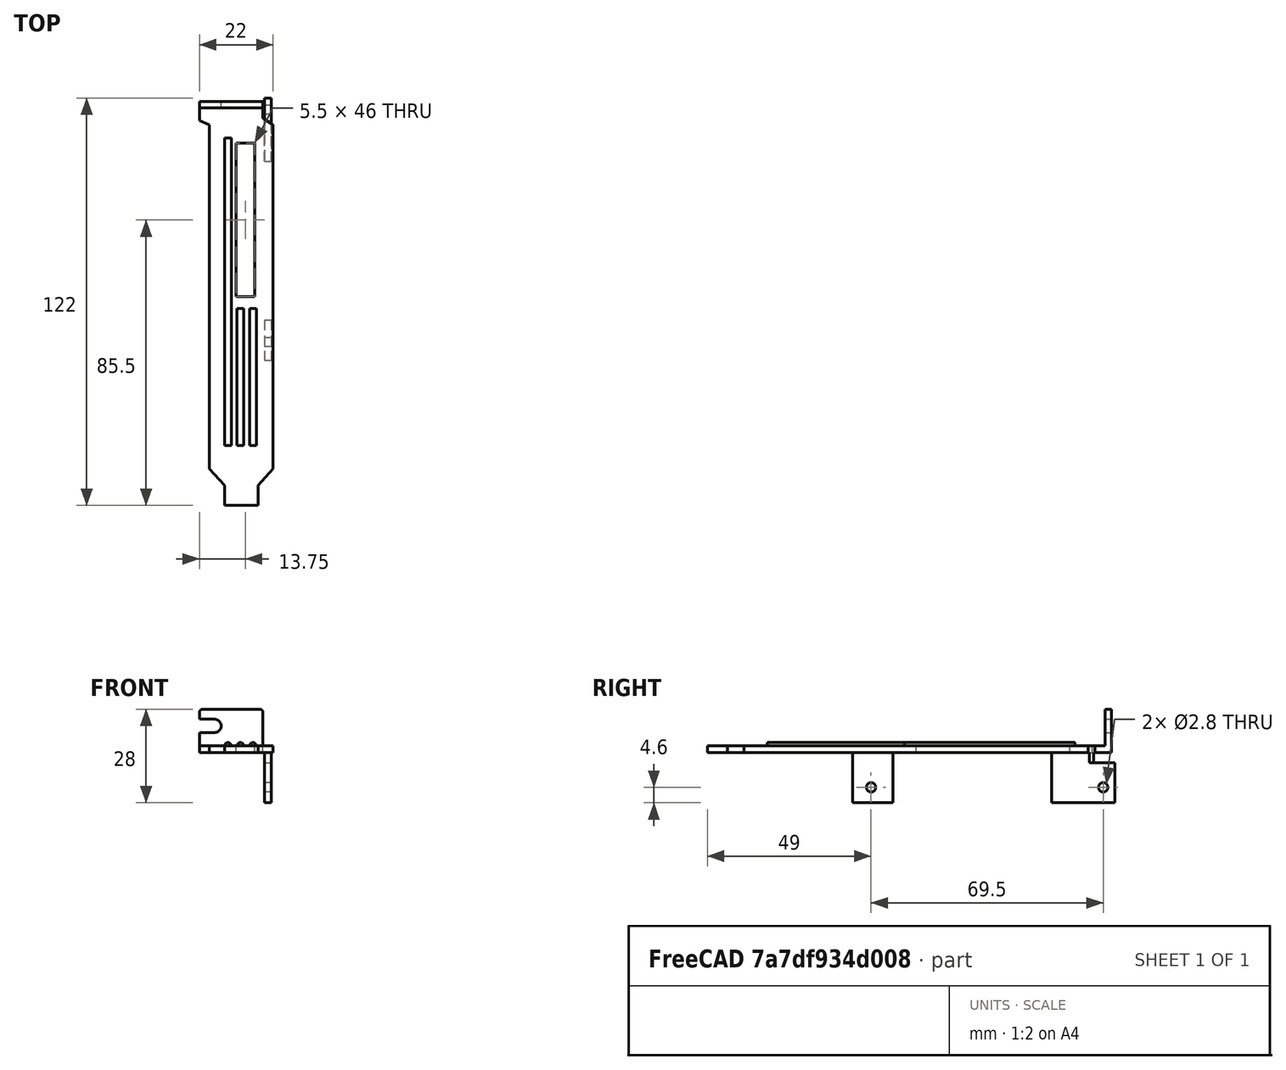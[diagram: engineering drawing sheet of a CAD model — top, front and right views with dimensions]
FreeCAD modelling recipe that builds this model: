
FCSTD DOCUMENT  (FreeCAD 0.20R29177 +426 (Git))
Label: A26x0 Slot Cover
License: All rights reserved
LicenseURL: http://en.wikipedia.org/wiki/All_rights_reserved
objects: PartDesign::AdditiveBox×5, PartDesign::SubtractiveWedge×5, PartDesign::SubtractiveCylinder×3, PartDesign::AdditiveCylinder×3, PartDesign::SubtractiveBox×2, PartDesign::Fillet×1, PartDesign::Body×1
note: 39 computed .brp shape members not serialized (recipe doc carries the construction recipe); baked Part::Feature solids carry a one-line shape summary decoded from their .brp

FEATURE [PartDesign::AdditiveBox] Box
  AttacherType = Attacher::AttachEngine3D
  AttachmentOffset = pos=(-9.5,-60,-1) rot=(0,0,1;0rad)
  Height = 2
  Length = 19
  MapMode = 5
  Placement = pos=(-9.5,-60,-1) rot=(0,0,1;0rad)
  Refine = true
  Support = -> [XY_Plane]
  Width = 114
FEATURE [PartDesign::SubtractiveWedge] Wedge
  AttacherType = Attacher::AttachEngine3D
  AttachmentOffset = pos=(5,-54,-1) rot=(0,0,-1;1.5708rad)
  BaseFeature = -> Box
  MapMode = 5
  Placement = pos=(5,-54,-1) rot=(0,0,-1;1.5708rad)
  Refine = true
  Support = -> [XY_Plane]
  X2max = 7
  X2min = -5
  Xmax = 7
  Xmin = 0
  Ymax = 4.5
  Ymin = 0
  Z2max = 5
  Z2min = 0
  Zmax = 5
  Zmin = 0
FEATURE [PartDesign::SubtractiveWedge] Wedge001
  AttacherType = Attacher::AttachEngine3D
  AttachmentOffset = pos=(5,-54,-1) rot=(0,0,-1;1.5708rad)
  BaseFeature = -> Wedge
  MapMode = 2
  Placement = pos=(-5,-54,1) rot=(-0.707107,0.707107,0;3.14159rad)
  Refine = true
  Support = -> [XY_Plane]
  X2max = 7
  X2min = -5
  Xmax = 7
  Xmin = 0
  Ymax = 4.5
  Ymin = 0
  Z2max = 5
  Z2min = 0
  Zmax = 5
  Zmin = 0
FEATURE [PartDesign::AdditiveBox] Box001
  AttacherType = Attacher::AttachEngine3D
  AttachmentOffset = pos=(-12.5,54,-1) rot=(0,0,1;0rad)
  BaseFeature = -> Wedge001
  Height = 2
  Length = 22
  MapMode = 5
  Placement = pos=(-12.5,54,-1) rot=(0,0,1;0rad)
  Refine = true
  Support = -> [XY_Plane]
  Width = 7
FEATURE [PartDesign::SubtractiveWedge] Wedge002
  AttacherType = Attacher::AttachEngine3D
  AttachmentOffset = pos=(6.5,60,-4) rot=(0,0,-1;1.5708rad)
  BaseFeature = -> Box001
  MapMode = 5
  Placement = pos=(6.5,60,-4) rot=(0,0,-1;1.5708rad)
  Refine = true
  Support = -> [XY_Plane]
  X2max = 6
  X2min = -1
  Xmax = 4
  Xmin = -1
  Ymax = 3
  Ymin = 0
  Z2max = 5
  Z2min = 0
  Zmax = 5
  Zmin = 0
FEATURE [PartDesign::SubtractiveWedge] Wedge003
  AttacherType = Attacher::AttachEngine3D
  AttachmentOffset = pos=(-19.5,54,-1) rot=(0,0,1;0rad)
  BaseFeature = -> Wedge002
  MapMode = 5
  Placement = pos=(-19.5,54,-1) rot=(0,0,1;0rad)
  Refine = true
  Support = -> [XY_Plane]
  X2max = 5
  X2min = 0
  Xmax = 10
  Xmin = 0
  Ymax = 2
  Ymin = 0
  Z2max = 2
  Z2min = 0
  Zmax = 2
  Zmin = 0
FEATURE [PartDesign::AdditiveBox] Box002
  AttacherType = Attacher::AttachEngine3D
  AttachmentOffset = pos=(-12.5,59,0) rot=(0,0,1;0rad)
  BaseFeature = -> Wedge003
  Height = 12
  Length = 19
  MapMode = 5
  Placement = pos=(-12.5,59,0) rot=(0,0,1;0rad)
  Refine = true
  Support = -> [XY_Plane]
  Width = 2
FEATURE [PartDesign::SubtractiveCylinder] Cylinder
  Angle = 360
  AttacherType = Attacher::AttachEngine3D
  AttachmentOffset = pos=(-8,7,-61) rot=(0,0,1;0rad)
  BaseFeature = -> Box002
  FirstAngle = 0
  Height = 2
  MapMode = 3
  Placement = pos=(-8,61,7) rot=(1,0,0;1.5708rad)
  Radius = 2
  Refine = true
  SecondAngle = 0
  Support = -> [XY_Plane]
FEATURE [PartDesign::SubtractiveBox] Box003
  AttacherType = Attacher::AttachEngine3D
  AttachmentOffset = pos=(-13,59,5) rot=(0,0,1;0rad)
  BaseFeature = -> Cylinder
  Height = 4
  Length = 5
  MapMode = 5
  Placement = pos=(-13,59,5) rot=(0,0,1;0rad)
  Refine = true
  Support = -> [XY_Plane]
  Width = 2
FEATURE [PartDesign::Fillet] Fillet
  Base = -> Box003 [Edge46,Edge54]
  BaseFeature = -> Box003
  Placement = pos=(-13,59,5) rot=(0,0,1;0rad)
  Radius = 1
  SupportTransform = false
  UseAllEdges = false
FEATURE [PartDesign::AdditiveCylinder] Cylinder001
  Angle = 180
  AttacherType = Attacher::AttachEngine3D
  AttachmentOffset = pos=(-0.25,1,1) rot=(0,0,1;0rad)
  BaseFeature = -> Fillet
  FirstAngle = 0
  Height = 41
  MapMode = 5
  Placement = pos=(-0.25,-1,1) rot=(1,0,0;1.5708rad)
  Radius = 1
  Refine = true
  SecondAngle = 0
  Support = -> [XZ_Plane]
FEATURE [PartDesign::AdditiveCylinder] Cylinder002
  Angle = 180
  AttacherType = Attacher::AttachEngine3D
  AttachmentOffset = pos=(3.5,1,1) rot=(0,0,1;0rad)
  BaseFeature = -> Cylinder001
  FirstAngle = 0
  Height = 41
  MapMode = 5
  Placement = pos=(3.5,-1,1) rot=(1,0,0;1.5708rad)
  Radius = 1
  Refine = true
  SecondAngle = 0
  Support = -> [XZ_Plane]
FEATURE [PartDesign::AdditiveCylinder] Cylinder003
  Angle = 180
  AttacherType = Attacher::AttachEngine3D
  AttachmentOffset = pos=(-4,1,-50) rot=(0,0,1;0rad)
  BaseFeature = -> Cylinder002
  FirstAngle = 0
  Height = 92
  MapMode = 5
  Placement = pos=(-4,50,1) rot=(1,0,0;1.5708rad)
  Radius = 1
  Refine = true
  SecondAngle = 0
  Support = -> [XZ_Plane]
FEATURE [PartDesign::AdditiveBox] Box004  label="UpperBrace"
  AttacherType = Attacher::AttachEngine3D
  AttachmentOffset = pos=(7,43,-16) rot=(0,0,1;0rad)
  BaseFeature = -> Cylinder003
  Height = 17
  Length = 2
  MapMode = 2
  Placement = pos=(7,43,-16) rot=(0,0,1;0rad)
  Refine = true
  Support = -> [XY_Plane]
  Width = 19
FEATURE [PartDesign::AdditiveBox] Box005  label="LowerBrace"
  AttacherType = Attacher::AttachEngine3D
  AttachmentOffset = pos=(-16.5,-16,7) rot=(0,0,1;0rad)
  BaseFeature = -> Box004
  Height = 2
  Length = 12
  MapMode = 2
  Placement = pos=(7,-16.5,-16) rot=(0.57735,0.57735,0.57735;2.0944rad)
  Refine = true
  Support = -> [YZ_Plane]
  Width = 17
FEATURE [PartDesign::SubtractiveCylinder] Cylinder005  label="LowerBraceHole"
  Angle = 360
  AttacherType = Attacher::AttachEngine3D
  AttachmentOffset = pos=(-11,-11.4,7) rot=(0,0,1;0rad)
  BaseFeature = -> Box005
  FirstAngle = 0
  Height = 2
  MapMode = 2
  Placement = pos=(7,-11,-11.4) rot=(0.57735,0.57735,0.57735;2.0944rad)
  Radius = 1.4
  Refine = true
  SecondAngle = 0
  Support = -> [YZ_Plane]
FEATURE [PartDesign::SubtractiveBox] Box006  label="CF Slot"
  AttacherType = Attacher::AttachEngine3D
  AttachmentOffset = pos=(-59.5,-8.5,-3) rot=(0,0,1;0rad)
  BaseFeature = -> Cylinder005
  Height = 5
  Length = 46
  MapMode = 5
  Placement = pos=(-1.5,48.5,-2) rot=(0,0,-1;1.5708rad)
  Support = -> [Cylinder005]
  Width = 5.5
FEATURE [PartDesign::SubtractiveCylinder] Cylinder006  label="UpperBraceHole"
  Angle = 360
  AttacherType = Attacher::AttachEngine3D
  AttachmentOffset = pos=(58.5,-11.4,7) rot=(0,0,1;0rad)
  BaseFeature = -> Box006
  FirstAngle = 0
  Height = 2
  MapMode = 5
  Placement = pos=(7,58.5,-11.4) rot=(0.57735,0.57735,0.57735;2.0944rad)
  Radius = 1.4
  SecondAngle = 0
  Support = -> [YZ_Plane]
FEATURE [PartDesign::SubtractiveWedge] Wedge004
  AttacherType = Attacher::AttachEngine3D
  AttachmentOffset = pos=(6.5,60,-4) rot=(0,0,-1;1.5708rad)
  BaseFeature = -> Cylinder006
  MapMode = 5
  Placement = pos=(6.5,60,-4) rot=(0,0,-1;1.5708rad)
  Support = -> [XY_Plane]
  X2max = 6
  X2min = -2
  Xmax = 4
  Xmin = -2
  Ymax = 3
  Ymin = 0
  Z2max = 5
  Z2min = 0
  Zmax = 5
  Zmin = 0
FEATURE [PartDesign::Body] Body  label="Amiga-EATX-Slot-Bracket"
  Group = -> [Box,Wedge,Wedge001,Box001,Wedge002,Wedge003,Box002,Cylinder,Box003,Fillet,Cylinder001,Cylinder002,Cylinder003,Box004,Box005,Cylinder005,Box006,Cylinder006,Wedge004]
  Origin = -> Origin
  Tip = -> Wedge004
